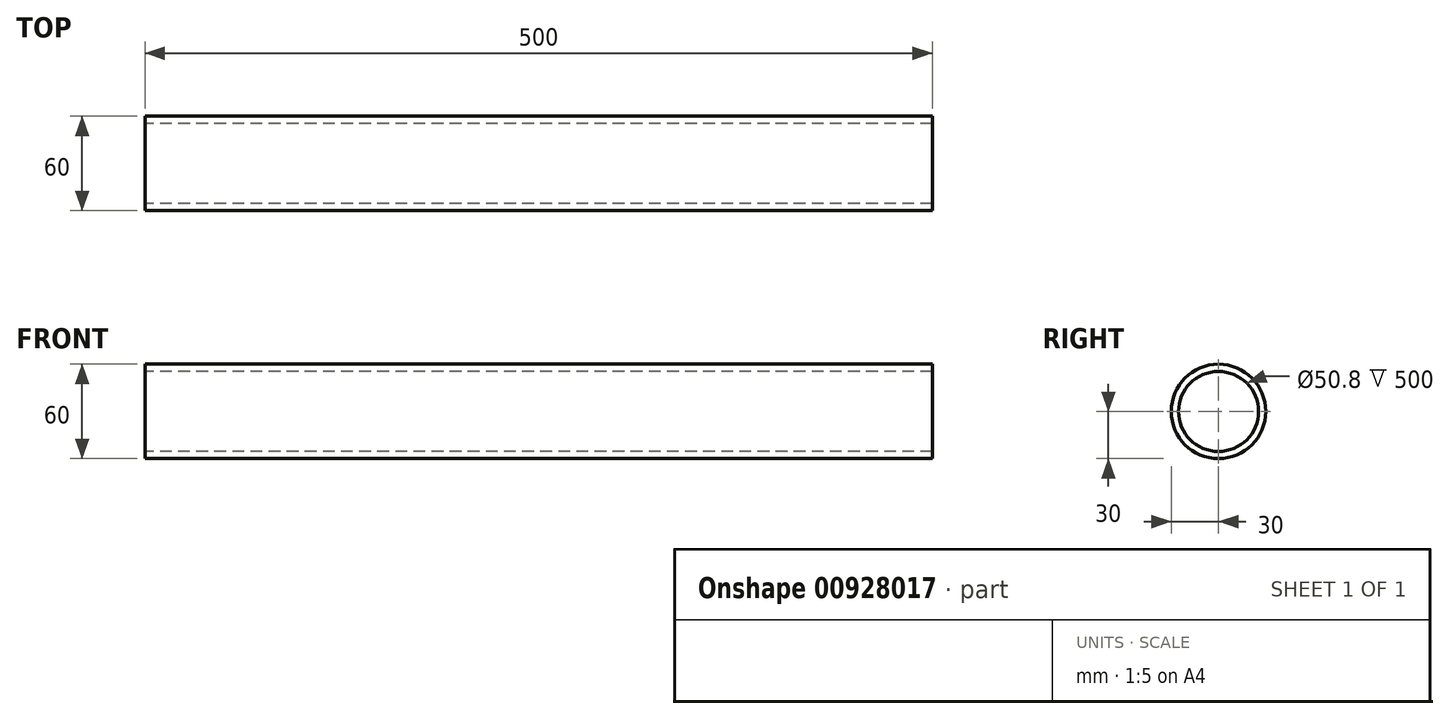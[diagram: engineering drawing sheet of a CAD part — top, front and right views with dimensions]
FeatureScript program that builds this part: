
annotation { "Feature Type Name" : "Feature", "Feature Type Description" : "" }
export const myFeature = defineFeature(function(context is Context, id is Id, definition is map)
    precondition{}
    {
        {
            var Q0;
            Q0=qCreatedBy(makeId("Right.planeOp"),FACE);
            var sketch = newSketch(context, id + "F0", { "sketchPlane" : qUnion([Q0])});
            skCircle(sketch, "E0", {"center": v(0, 0) * mm, "radius": 30 * mm});
            skCircle(sketch, "E1", {"center": v(0, 0) * mm, "radius": 25.4 * mm});
            skSolve(sketch);
        }
        {
            var Q0;
            Q0=qSketchRegion(id+"F0",true);
            extrude(context, id + "F1", {"entities" : qUnion([Q0]), "depth" : 500 * mm, "offsetDistance" : 25 * mm});
        }
    });
